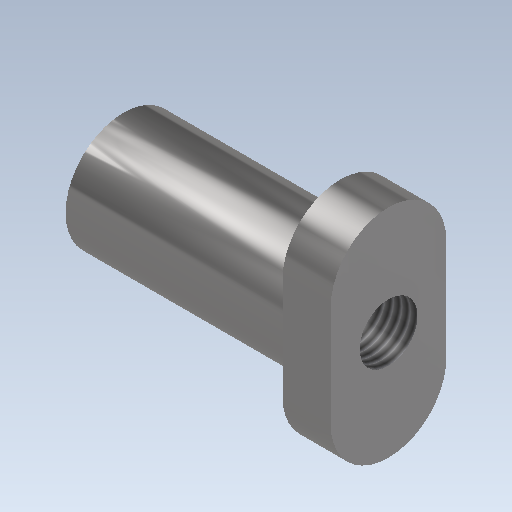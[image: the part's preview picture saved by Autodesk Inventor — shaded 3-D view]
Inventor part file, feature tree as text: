
AUTODESK INVENTOR PART (.ipt)
format: ipt  version: 2021.3 (Build 253353000, 353)  size: 164,864 bytes
history: native  units: mm
features: extrude x2, sketch x2, fillet x1, thread x1
ambient origin geometry x8: Origin, YZ Plane, XZ Plane, XY Plane, X Axis, Y Axis, Z Axis, Center Point
bodies: Solid1 (feature_tree)
feature tree (6):
  extrude  "Extrusion1"  Depth=24.0mm
  extrude  "Extrusion2"  Depth=45.0mm
  fillet  "Fillet1"  Radius=10.0mm
  thread  "Thread1"  [1 undecoded]
  sketch  "Sketch1"  dims[d0=12.0mm d1=24.0mm]
  sketch  "Sketch2"  dims[d2=45.0mm d3=0.0mm d4=45.0mm d5=10.0mm d6=0.0mm d7=12.0mm d8=10.0mm d9=0.0mm]
note: 1 required parameter value undecoded (feature->parameter linkage not recoverable at this tier; creation-order binding heuristic only, values carry confidence <= 0.55)
